# Revit family: DC_Rheem_PLM_CPI7_BackToBack
name_source: partatom
category: Plumbing Fixtures
revit_build: Autodesk Revit 2018 (Build: 20170223_1515(x64)
units: mm (PartAtom-declared; Revit-internal decimal feet)

## family parameters
Cut with Voids When Loaded = No
Host = Face
Part Type = Normal
Room Calculation Point = No
Round Connector Dimension = Use Radius
Shared = No

## types (2) — shared parameters
Cold Water Pipe Diameter = 50 mm  [stored 0.164042 ft]
ColdWaterPipeRadius_ANZRS = 25 mm  [stored 0.082021 ft]
GasPipeDiameterD3_ANZRS = 50 mm  [stored 0.164042 ft]
GasPipeRadius_ANZRS = 25 mm  [stored 0.082021 ft]
HotWaterOutletDiameterD2_ANZRS = 50 mm  [stored 0.164042 ft]
HotWaterOutletRadius_ANZRS = 25 mm  [stored 0.082021 ft]
HotWaterReturnDiameterD1_ANZRS = 25 mm  [stored 0.082021 ft]
HotWaterReturnRadius_ANZRS = 12.5 mm  [stored 0.0410105 ft]
Length_ANZRS = 1440 mm  [stored 4.72441 ft]
Manufacturer = Rheem
Materials_ANZRS = Rheem - Antique White
Type Comments = 92L/min @ 50°C rise - Dual 50% capacity pump and controller included
URL = http://www.rheem.com.au
zero-valued in all types: Default Elevation

## per-type parameters (varying)
| type | Description | Model |
| Commpak - Gas Continuous Flow - Indoor - 1435 MJ/h Natural gas free standing frame - back to back | Commpak - Gas Continuous Flow - Indoor - 1435 MJ/h Natural gas free standing frame - back to back | CPI07NB |
| Commpak - Gas Continuous Flow - Indoor - 1435 MJ/h Propane gas free standing frame - back to back | Commpak - Gas Continuous Flow - indoor - 1435 MJ/h Propane gas free standing frame - back to back | CPI07PB |

note: [stored X ft] marks values corroborated as IEEE doubles in the binary element streams (Revit-internal decimal feet)

## geometry (parser evidence)
native form markers: Sweep x29
no freeform markers — native parametric forms only
